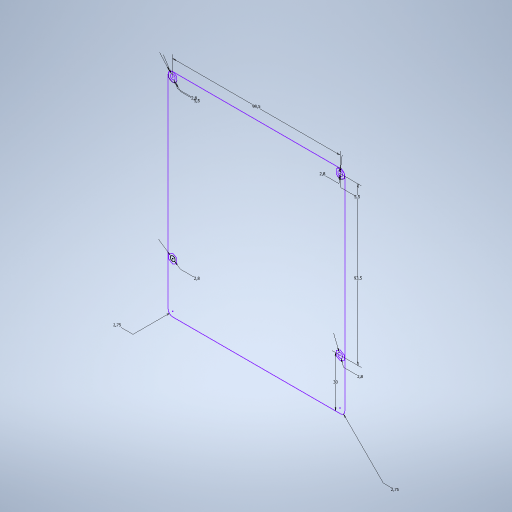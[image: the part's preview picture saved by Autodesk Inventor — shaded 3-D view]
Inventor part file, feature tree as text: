
AUTODESK INVENTOR PART (.ipt)
format: ipt  version: 2023 (Build 270158000, 158)  size: 252,928 bytes
history: native  units: mm
features: sketch x1
ambient origin geometry x8: Origin, YZ Plane, XZ Plane, XY Plane, X Axis, Y Axis, Z Axis, Center Point
feature tree (1):
  sketch  "Sketch1"  dims[d2=2.8mm d3=2.8mm d4=2.8mm d5=2.8mm d6=5.5mm d7=5.5mm d10=99.5mm d11=93.5mm d12=30.0mm d13=2.75mm d14=2.75mm]
